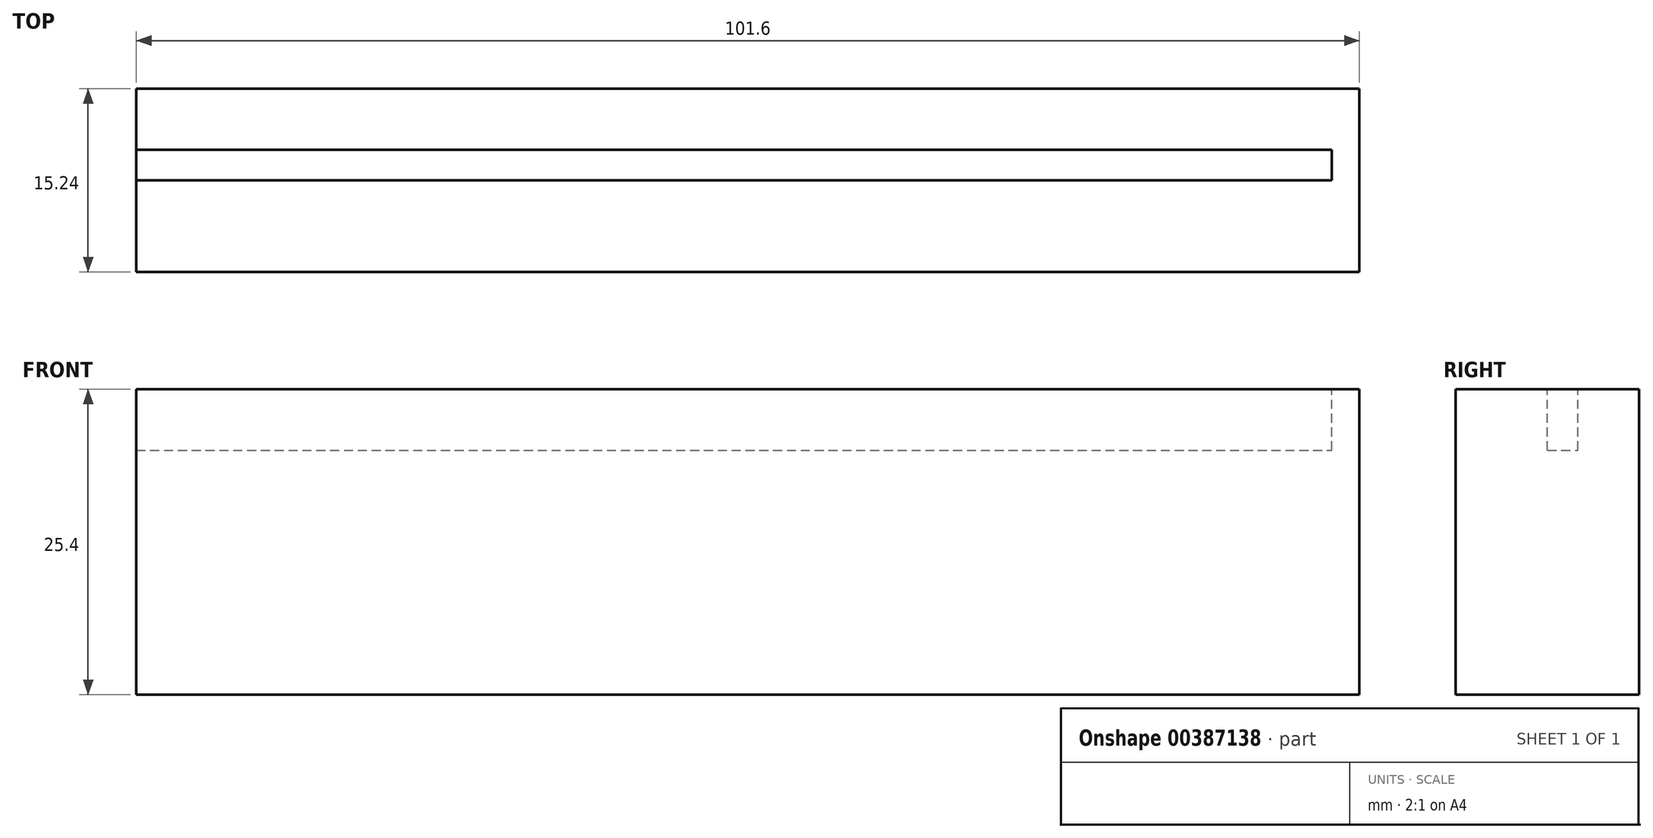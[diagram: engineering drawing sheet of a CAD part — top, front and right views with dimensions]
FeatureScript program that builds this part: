
annotation { "Feature Type Name" : "Feature", "Feature Type Description" : "" }
export const myFeature = defineFeature(function(context is Context, id is Id, definition is map)
    precondition{}
    {
        {
            var Q0;
            Q0=qCreatedBy(makeId("Front.planeOp"),FACE);
            var sketch = newSketch(context, id + "F0", { "sketchPlane" : qUnion([Q0])});
            skLineSegment(sketch, "E0.bottom", {"start": v(0, 0) * mm, "end": v(101.6, 0) * mm});
            skLineSegment(sketch, "E0.top", {"start": v(0, 25.4) * mm, "end": v(101.6, 25.4) * mm});
            skLineSegment(sketch, "E0.left", {"start": v(0, 0) * mm, "end": v(0, 25.4) * mm});
            skLineSegment(sketch, "E0.right", {"start": v(101.6, 0) * mm, "end": v(101.6, 25.4) * mm});
            skSolve(sketch);
        }
        {
            var Q0;
            Q0=makeQuery(id+"F0.imprint","IMPRINT",FACE,{"disambiguationData":[TD([[makeQuery(id+"F0.imprint","IMPRINT",EDGE,{"derivedFrom":sQuery(id+"F0.wireOp",EDGE,"E0.bottom")}),1.0]])]});
            extrude(context, id + "F1", {"entities" : qUnion([Q0]), "depth" : 15.24 * mm});
        }
        {
            var Q0;
            Q0=makeQuery(id+"F1.opExtrude","SWEPT_FACE",FACE,{"disambiguationData":[OSD([sQuery(id+"F0.wireOp",EDGE,"E0.top")])]});
            var sketch = newSketch(context, id + "F2", { "sketchPlane" : qUnion([Q0])});
            skLineSegment(sketch, "E1.bottom", {"start": v(0, -7.62) * mm, "end": v(99.3, -7.62) * mm});
            skLineSegment(sketch, "E1.top", {"start": v(0, -5.08) * mm, "end": v(99.3, -5.08) * mm});
            skLineSegment(sketch, "E1.left", {"start": v(0, -7.62) * mm, "end": v(0, -5.08) * mm});
            skLineSegment(sketch, "E1.right", {"start": v(99.3, -7.62) * mm, "end": v(99.3, -5.08) * mm});
            skSolve(sketch);
        }
        {
            var Q0;
            Q0 = qSketchRegion(id + "F2", true);
            extrude(context, id + "F3", {"entities" : qUnion([Q0]), "operationType" : NewBodyOperationType.REMOVE, "oppositeDirection" : true, "depth" : 5.08 * mm});
        }
        {
            var Q0;
            Q0=makeQuery(id+"F1.opExtrude","SWEPT_FACE",FACE,{"disambiguationData":[OSD([sQuery(id+"F0.wireOp",EDGE,"E0.right")])]});
            var sketch = newSketch(context, id + "F4", { "sketchPlane" : qUnion([Q0])});
            skCircle(sketch, "E2", {"center": v(-7.62, 12.7) * mm, "radius": 1.27 * mm});
            skPoint(sketch, "E2.centerSnap0", {"position": v(0, 12.7) * mm});
            skPoint(sketch, "E2.centerSnap1", {"position": v(-7.62, 25.4) * mm});
            skSolve(sketch);
        }
        {
            var Q0;
            Q0=sQuery(id+"F4.wireOp",EDGE,"E2");
            extrude(context, id + "F5", {"bodyType" : ToolBodyType.SURFACE, "surfaceEntities" : qUnion([Q0]), "depth" : 2.54 * mm});
        }
    });
